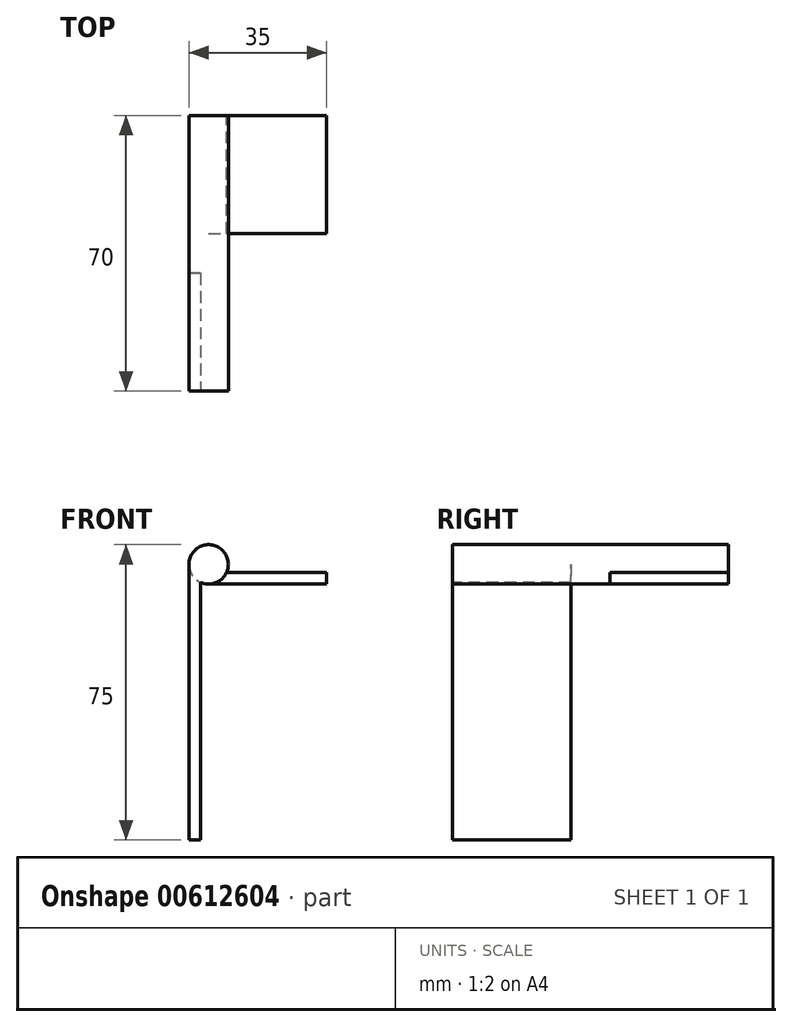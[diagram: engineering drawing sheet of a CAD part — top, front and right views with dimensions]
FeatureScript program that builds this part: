
annotation { "Feature Type Name" : "Feature", "Feature Type Description" : "" }
export const myFeature = defineFeature(function(context is Context, id is Id, definition is map)
    precondition{}
    {
        {
            var Q0;
            Q0=qCreatedBy(makeId("Front.planeOp"),FACE);
            var sketch = newSketch(context, id + "F0", { "sketchPlane" : qUnion([Q0])});
            skCircle(sketch, "E0", {"center": v(0, 0) * mm, "radius": 5 * mm});
            skLineSegment(sketch, "E1.0", {"start": v(0, -5) * mm, "end": v(30, -5) * mm});
            skLineSegment(sketch, "E2.0", {"start": v(0, -2) * mm, "end": v(30, -2) * mm});
            skLineSegment(sketch, "E3", {"start": v(0, -2) * mm, "end": v(0, -5) * mm});
            skLineSegment(sketch, "E4", {"start": v(30, -2) * mm, "end": v(30, -5) * mm});
            skLineSegment(sketch, "E5", {"start": v(-2, -70) * mm, "end": v(-5, -70) * mm});
            skSolve(sketch);
        }
        {
            var Q0;
            {var subQ0=sQuery(id+"F0.wireOp",EDGE,"E3");Q0=makeQuery(id+"F0.imprint","IMPRINT",FACE,{"disambiguationData":[TD([[makeQuery(id+"F0.imprint","IMPRINT",EDGE,{"derivedFrom":subQ0}),-1.0]])]});}
            var Q1;
            {var subQ0=sQuery(id+"F0.wireOp",EDGE,"ShSTM8aS-ZKQa-7d71-j1zm-0fq5bK1w7sQr");Q1=makeQuery(id+"F0.imprint","IMPRINT",FACE,{"disambiguationData":[TD([[makeQuery(id+"F0.imprint","IMPRINT",EDGE,{"derivedFrom":subQ0}),-1.0]])]});}
            var Q2;
            {var subQ0=sQuery(id+"F0.wireOp",EDGE,"E3");Q2=makeQuery(id+"F0.imprint","IMPRINT",FACE,{"disambiguationData":[TD([[makeQuery(id+"F0.imprint","IMPRINT",EDGE,{"derivedFrom":subQ0}),1.0]])]});}
            extrude(context, id + "F1", {"entities" : qUnion([Q0, Q1, Q2]), "depth" : 70 * mm, "offsetDistance" : 25.4 * mm});
        }
        {
            var Q0;
            {var subQ0=sQuery(id+"F0.wireOp",EDGE,"E1.0");Q0=makeQuery(id+"F0.imprint","IMPRINT",FACE,{"disambiguationData":[TD([[makeQuery(id+"F0.imprint","IMPRINT",EDGE,{"derivedFrom":subQ0}),1.0]])]});}
            extrude(context, id + "F2", {"entities" : qUnion([Q0]), "operationType" : NewBodyOperationType.ADD, "depth" : 30 * mm, "offsetDistance" : 25.4 * mm});
        }
        {
            var Q0;
            Q0=makeQuery(id+"F1.opExtrude","CAP_FACE",FACE,{"disambiguationData":[OSD([sQuery(id+"F0.wireOp",EDGE,"E0")])],"isStart":false});
            var sketch = newSketch(context, id + "F3", { "sketchPlane" : qUnion([Q0])});
            skLineSegment(sketch, "E6", {"start": v(-2, 0) * mm, "end": v(-2, -70) * mm});
            skLineSegment(sketch, "E7", {"start": v(-2, -70) * mm, "end": v(-5, -70) * mm});
            skLineSegment(sketch, "E8", {"start": v(-5, -70) * mm, "end": v(-5, 0) * mm});
            skLineSegment(sketch, "E9", {"start": v(-5, 0) * mm, "end": v(-2, 0) * mm});
            skSolve(sketch);
        }
        {
            var Q0;
            {var subQ0=sQuery(id+"F3.wireOp",EDGE,"E7");Q0=makeQuery(id+"F3.imprint","IMPRINT",FACE,{"disambiguationData":[TD([[makeQuery(id+"F3.imprint","IMPRINT",EDGE,{"derivedFrom":subQ0}),-1.0]])]});}
            extrude(context, id + "F4", {"entities" : qUnion([Q0]), "operationType" : NewBodyOperationType.ADD, "oppositeDirection" : true, "depth" : 30 * mm, "offsetDistance" : 25.4 * mm});
        }
    });
